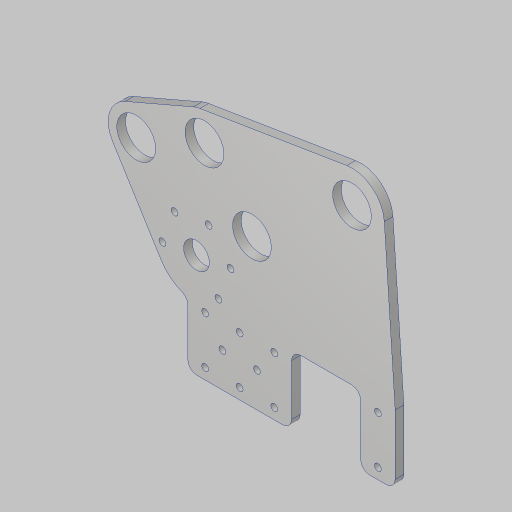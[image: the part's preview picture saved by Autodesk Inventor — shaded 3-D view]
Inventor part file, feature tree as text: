
AUTODESK INVENTOR PART (.ipt)
format: ipt  version: 2023.5 (Build 275446000, 446)  size: 269,312 bytes
history: native  units: in
note: dims shown in document units (in); Inventor stores cm internally (conversion verified against a paired STEP export)
features: sketch x3, extrude x3, hole x2, fillet x2, projected_geometry x1
ambient origin geometry x8: Origin, YZ Plane, XZ Plane, XY Plane, X Axis, Y Axis, Z Axis, Center Point
bodies: Solid1 (feature_tree)
feature tree (11):
  sketch  "Sketch1"  dims[d0=6.0in d1=2.0in]
  sketch  "Sketch2"  dims[d2=1.375in d3=0.5in d4=1.25in]
  extrude  "Extrusion1"  Depth=2.0in
  hole  "Hole1"  [1 undecoded]
  fillet  "Fillet1"  Radius=1.25in
  sketch  "Sketch4"  dims[d5=1.25in d6=1.375in d7=1.0in d8=0.375in d9=0.5in d10=0.5in d11=0.5in d12=0.5in d13=0.5in d14=4.38in d15=5.0in d16=3.0in d17=1.125in d18=0.375in d20=0.375in d21=0.375in d22=0.25in d23=0.0in d24=0.201in d25=0.75in d26=0.375in d27=0.25in d28=0.5635in d29=1.0in d30=0.8108in d31=6.5in d32=0.75in d33=0.26in d45=2.0in d46=2.4in d47=0.75in d48=0.5in d49=3.6in d50=0.25in d52=8.0in d53=2.0in d54=3.0in d55=1.125in d56=0.25in d57=1.0in d58=3.3in d59=2.275in d60=1.0in d61=3.3in d62=2.9288in d64=0.25in d65=0.25in d66=1.0in d67=0.0in d68=2.3622in d70=360.0deg d72=0.0in d73=0.0in d74=0.201in d75=0.75in d76=0.385in d77=0.25in d78=0.5635in d79=1.0in d80=0.8108in d82=3.342in d83=0.58in d85=0.26in d86=1.114in d92=6.3055in d93=5.834in d94=1.5551in]
  extrude  "Extrusion3"  Depth=0.26in
  extrude  "Extrusion4"  Depth=1.0in
  hole  "Hole2"  [1 undecoded]
  fillet  "Fillet4"  Radius=0.5in
  projected_geometry  "Project Cut Edges2"
note: 2 required parameter values undecoded (feature->parameter linkage not recoverable at this tier; creation-order binding heuristic only, values carry confidence <= 0.55)
